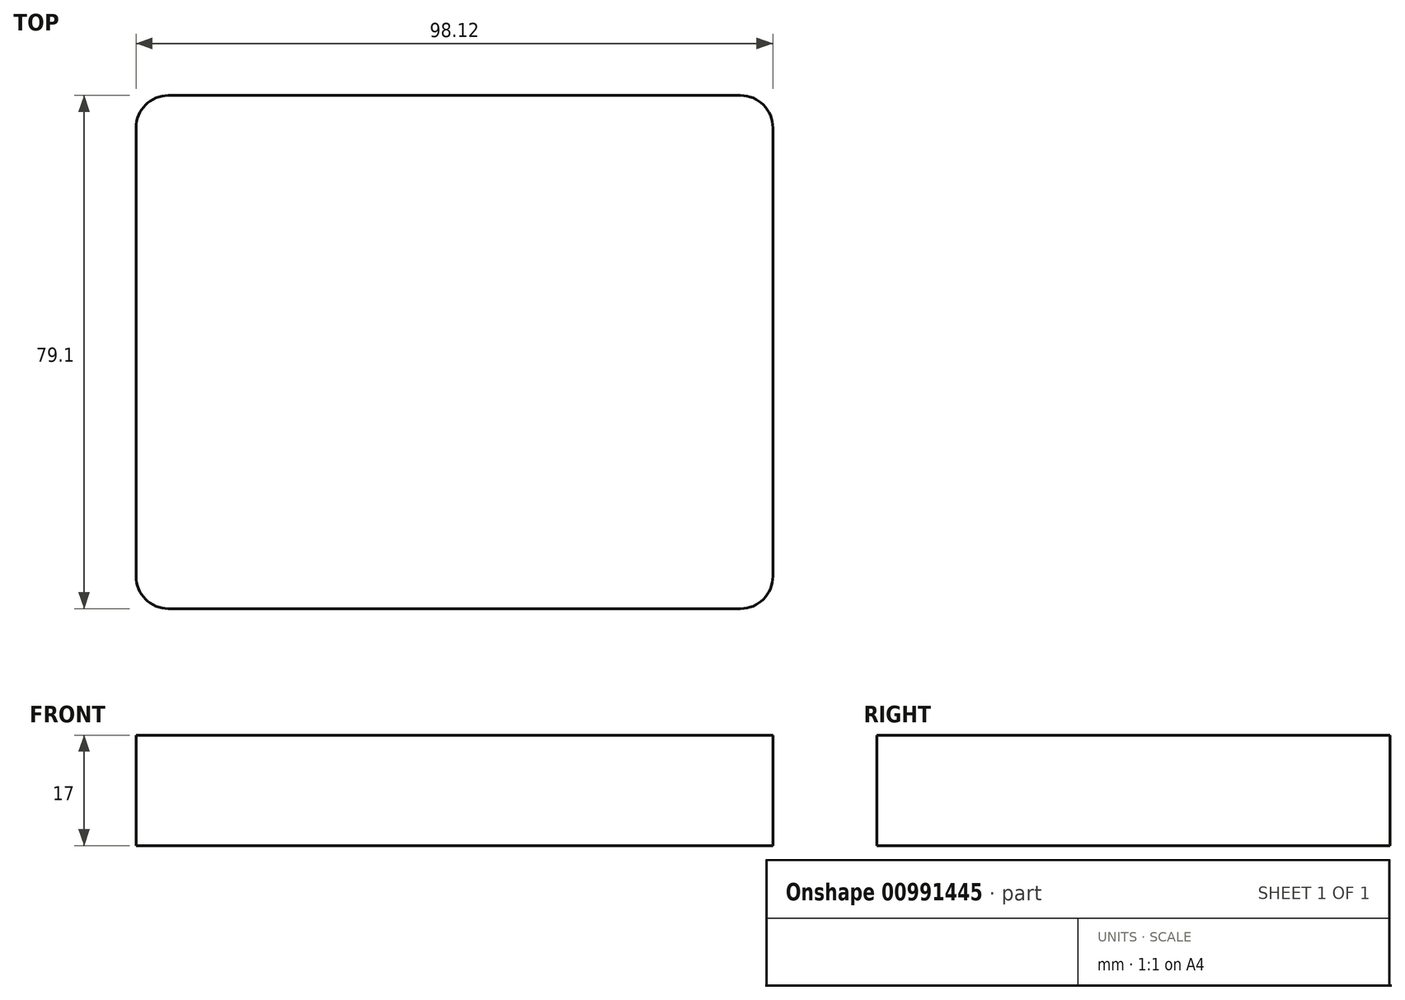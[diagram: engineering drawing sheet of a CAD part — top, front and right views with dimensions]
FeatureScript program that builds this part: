
annotation { "Feature Type Name" : "Feature", "Feature Type Description" : "" }
export const myFeature = defineFeature(function(context is Context, id is Id, definition is map)
    precondition{}
    {
        {
            var Q0;
            Q0=qCreatedBy(makeId("Top.planeOp"),FACE);
            var sketch = newSketch(context, id + "F0", { "sketchPlane" : qUnion([Q0])});
            skLineSegment(sketch, "E0.bottom", {"start": v(49.06, -39.55) * mm, "end": v(-49.06, -39.55) * mm});
            skLineSegment(sketch, "E0.top", {"start": v(49.06, 39.55) * mm, "end": v(-49.06, 39.55) * mm});
            skLineSegment(sketch, "E0.left", {"start": v(49.06, -39.55) * mm, "end": v(49.06, 39.55) * mm});
            skLineSegment(sketch, "E0.right", {"start": v(-49.06, -39.55) * mm, "end": v(-49.06, 39.55) * mm});
            skPoint(sketch, "E0.middle", {"position": v(0, 0) * mm});
            skSolve(sketch);
        }
        {
            var Q0;
            Q0=makeQuery(id+"F0.imprint","IMPRINT",FACE,{"disambiguationData":[TD([[makeQuery(id+"F0.imprint","IMPRINT",EDGE,{"derivedFrom":sQuery(id+"F0.wireOp",EDGE,"E0.bottom")}),-1.0]])]});
            extrude(context, id + "F1", {"entities" : qUnion([Q0]), "depth" : 2 * mm, "offsetDistance" : 25 * mm});
        }
        {
            var Q0;
            Q0=makeQuery(id+"F1.opExtrude","SWEPT_EDGE",EDGE,{"disambiguationData":[OSD([sQuery(id+"F0.wireOp",EDGE,"E0.bottom"),sQuery(id+"F0.wireOp",EDGE,"E0.right")])]});
            var Q1;
            Q1=makeQuery(id+"F1.opExtrude","SWEPT_EDGE",EDGE,{"disambiguationData":[OSD([sQuery(id+"F0.wireOp",EDGE,"E0.bottom"),sQuery(id+"F0.wireOp",EDGE,"E0.left")])]});
            var Q2;
            Q2=makeQuery(id+"F1.opExtrude","SWEPT_EDGE",EDGE,{"disambiguationData":[OSD([sQuery(id+"F0.wireOp",EDGE,"E0.top"),sQuery(id+"F0.wireOp",EDGE,"E0.left")])]});
            var Q3;
            Q3=makeQuery(id+"F1.opExtrude","SWEPT_EDGE",EDGE,{"disambiguationData":[OSD([sQuery(id+"F0.wireOp",EDGE,"E0.top"),sQuery(id+"F0.wireOp",EDGE,"E0.right")])]});
            fillet(context, id + "F2", {"entities" : qUnion([Q0, Q1, Q2, Q3]), "radius" : 5 * mm, "tangentPropagation" : true, "allowEdgeOverflow" : false});
        }
        {
            var Q0;
            Q0=makeQuery(id+"F1.opExtrude","CAP_FACE",FACE,{"disambiguationData":[OSD([sQuery(id+"F0.wireOp",EDGE,"E0.bottom"),sQuery(id+"F0.wireOp",EDGE,"E0.top"),sQuery(id+"F0.wireOp",EDGE,"E0.left"),sQuery(id+"F0.wireOp",EDGE,"E0.right")])],"isStart":false});
            extrude(context, id + "F3", {"entities" : qUnion([Q0]), "operationType" : NewBodyOperationType.ADD, "depth" : 15 * mm, "offsetDistance" : 25 * mm});
        }
    });
